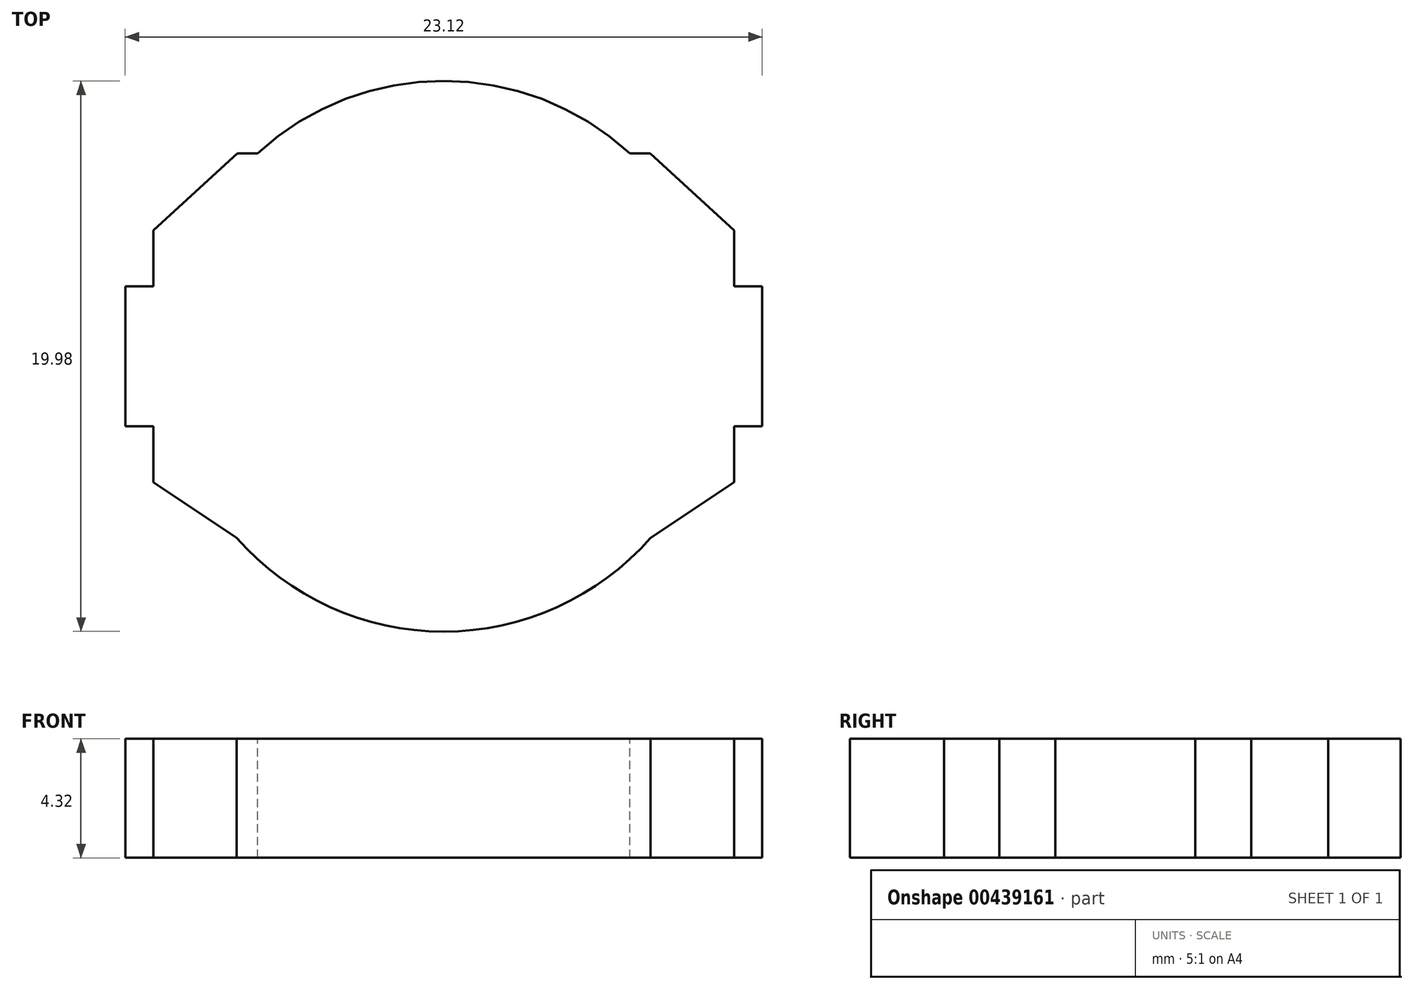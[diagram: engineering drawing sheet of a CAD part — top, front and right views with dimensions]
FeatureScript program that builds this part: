
annotation { "Feature Type Name" : "Feature", "Feature Type Description" : "" }
export const myFeature = defineFeature(function(context is Context, id is Id, definition is map)
    precondition{}
    {
        {
            var Q0;
            Q0=qCreatedBy(makeId("Top.planeOp"),FACE);
            var sketch = newSketch(context, id + "F0", { "sketchPlane" : qUnion([Q0])});
            skPoint(sketch, "E0.middle", {"position": v(0, 0) * mm});
            skLineSegment(sketch, "E1.bottom", {"start": v(-11.56, 2.54) * mm, "end": v(-10.54, 2.54) * mm});
            skLineSegment(sketch, "E1.top", {"start": v(-11.56, -2.54) * mm, "end": v(-10.54, -2.54) * mm});
            skLineSegment(sketch, "E1.left", {"start": v(-11.56, 2.54) * mm, "end": v(-11.56, -2.54) * mm});
            skLineSegment(sketch, "E2.trimOffspring", {"start": v(-10.54, -2.54) * mm, "end": v(-10.54, -4.57) * mm});
            skLineSegment(sketch, "E3", {"start": v(-10.54, 4.57) * mm, "end": v(-10.54, 2.54) * mm});
            skLineSegment(sketch, "E4", {"start": v(-10.54, 4.57) * mm, "end": v(-7.5, 7.37) * mm});
            skLineSegment(sketch, "E5", {"start": v(-7.5, 7.37) * mm, "end": v(0, 7.37) * mm});
            skLineSegment(sketch, "E6", {"start": v(-10.54, -4.57) * mm, "end": v(-5.59, -7.87) * mm});
            skLineSegment(sketch, "E7", {"start": v(-5.59, -7.87) * mm, "end": v(0, -7.87) * mm});
            skLineSegment(sketch, "E8.MirrorCS", {"start": v(7.5, 7.37) * mm, "end": v(0, 7.37) * mm});
            skLineSegment(sketch, "E9.MirrorCS", {"start": v(10.54, 4.57) * mm, "end": v(7.5, 7.37) * mm});
            skLineSegment(sketch, "E10.MirrorCS", {"start": v(10.54, 4.57) * mm, "end": v(10.54, 2.54) * mm});
            skLineSegment(sketch, "E11.MirrorCS", {"start": v(11.56, 2.54) * mm, "end": v(10.54, 2.54) * mm});
            skLineSegment(sketch, "E12.MirrorCS", {"start": v(11.56, 2.54) * mm, "end": v(11.56, -2.54) * mm});
            skLineSegment(sketch, "E13.MirrorCS", {"start": v(11.56, -2.54) * mm, "end": v(10.54, -2.54) * mm});
            skLineSegment(sketch, "E14.MirrorCS", {"start": v(10.54, -2.54) * mm, "end": v(10.54, -4.57) * mm});
            skLineSegment(sketch, "E15.MirrorCS", {"start": v(10.54, -4.57) * mm, "end": v(5.59, -7.87) * mm});
            skLineSegment(sketch, "E16.MirrorCS", {"start": v(5.59, -7.87) * mm, "end": v(0, -7.87) * mm});
            skArc(sketch, "E17", {"start": v(-7.52, -6.59) * mm, "mid": v(0, -10) * mm, "end": v(7.52, -6.59) * mm});
            skArc(sketch, "E18.trimOffspring", {"start": v(6.76, 7.37) * mm, "mid": v(0, 10) * mm, "end": v(-6.76, 7.37) * mm});
            skSolve(sketch);
        }
        {
            var Q0;
            Q0 = qSketchRegion(id + "F0", true);
            extrude(context, id + "F1", {"entities" : qUnion([Q0]), "oppositeDirection" : true, "depth" : 4.32 * mm});
        }
    });
